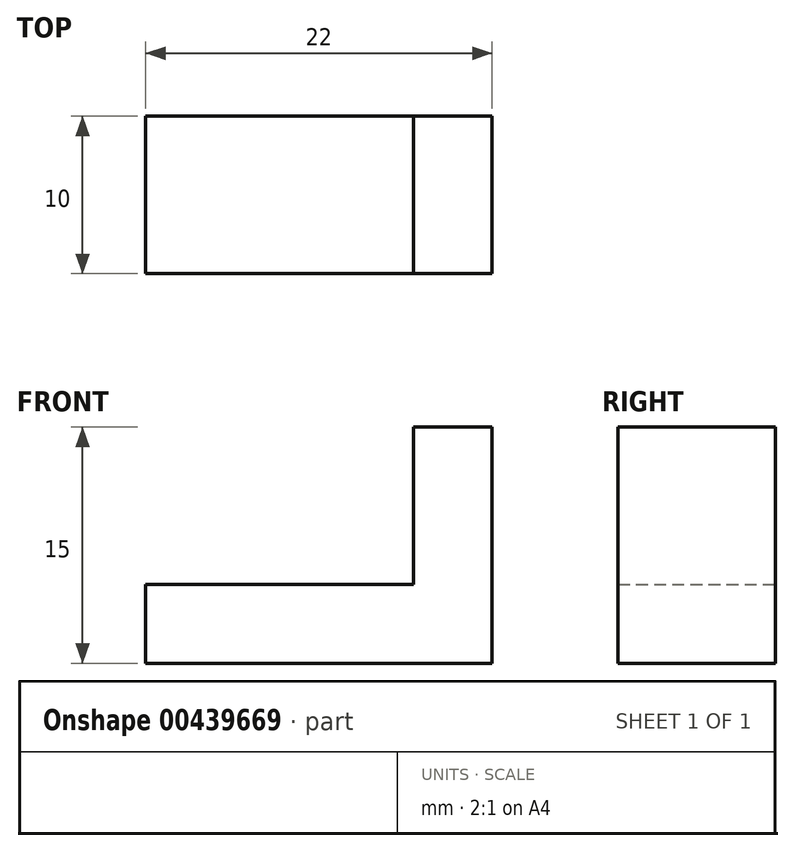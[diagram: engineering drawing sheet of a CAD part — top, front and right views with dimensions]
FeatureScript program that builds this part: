
annotation { "Feature Type Name" : "Feature", "Feature Type Description" : "" }
export const myFeature = defineFeature(function(context is Context, id is Id, definition is map)
    precondition{}
    {
        {
            assignVariable(context, id + "F0", {"name" : "height_bottom", "anyValue" : 5 * mm});
        }
        {
            assignVariable(context, id + "F1", {"name" : "height_top", "anyValue" : 15 * mm - getVariable(context, 'height_bottom')});
        }
        {
            var Q0;
            Q0=qCreatedBy(makeId("Top.planeOp"),FACE);
            var sketch = newSketch(context, id + "F2", { "sketchPlane" : qUnion([Q0])});
            skLineSegment(sketch, "E0", {"start": v(0, 0) * mm, "end": v(22, 0) * mm});
            skLineSegment(sketch, "E1", {"start": v(22, 0) * mm, "end": v(22, 10) * mm});
            skLineSegment(sketch, "E2", {"start": v(22, 10) * mm, "end": v(0, 10) * mm});
            skLineSegment(sketch, "E3", {"start": v(0, 10) * mm, "end": v(0, 0) * mm});
            skSolve(sketch);
        }
        {
            var Q0;
            Q0 = qSketchRegion(id + "F2", true);
            var Q1;
            Q1=makeQuery(id+"F2.imprint","IMPRINT",FACE,{"disambiguationData":[TD([[makeQuery(id+"F2.imprint","IMPRINT",EDGE,{"derivedFrom":sQuery(id+"F2.wireOp",EDGE,"E0")}),1.0]])]});
            extrude(context, id + "F3", {"entities" : qUnion([Q0, Q1]), "depth" : getVariable(context, 'height_bottom')});
        }
        {
            var Q0;
            Q0=makeQuery(id+"F3.opExtrude","CAP_FACE",FACE,{"disambiguationData":[OSD([sQuery(id+"F2.wireOp",EDGE,"E0"),sQuery(id+"F2.wireOp",EDGE,"E1"),sQuery(id+"F2.wireOp",EDGE,"E2"),sQuery(id+"F2.wireOp",EDGE,"E3")])],"isStart":false});
            var sketch = newSketch(context, id + "F4", { "sketchPlane" : qUnion([Q0])});
            skLineSegment(sketch, "E4", {"start": v(22, 10) * mm, "end": v(22, 0) * mm});
            skLineSegment(sketch, "E5", {"start": v(22, 0) * mm, "end": v(17, 0) * mm});
            skLineSegment(sketch, "E6", {"start": v(17, 0) * mm, "end": v(17, 10) * mm});
            skLineSegment(sketch, "E7", {"start": v(17, 10) * mm, "end": v(22, 10) * mm});
            skSolve(sketch);
        }
        {
            var Q0;
            Q0=makeQuery(id+"F4.imprint","IMPRINT",FACE,{"disambiguationData":[TD([[makeQuery(id+"F4.imprint","IMPRINT",EDGE,{"derivedFrom":sQuery(id+"F4.wireOp",EDGE,"E4")}),1.0]])]});
            extrude(context, id + "F5", {"entities" : qUnion([Q0]), "operationType" : NewBodyOperationType.ADD, "depth" : getVariable(context, 'height_top')});
        }
    });
